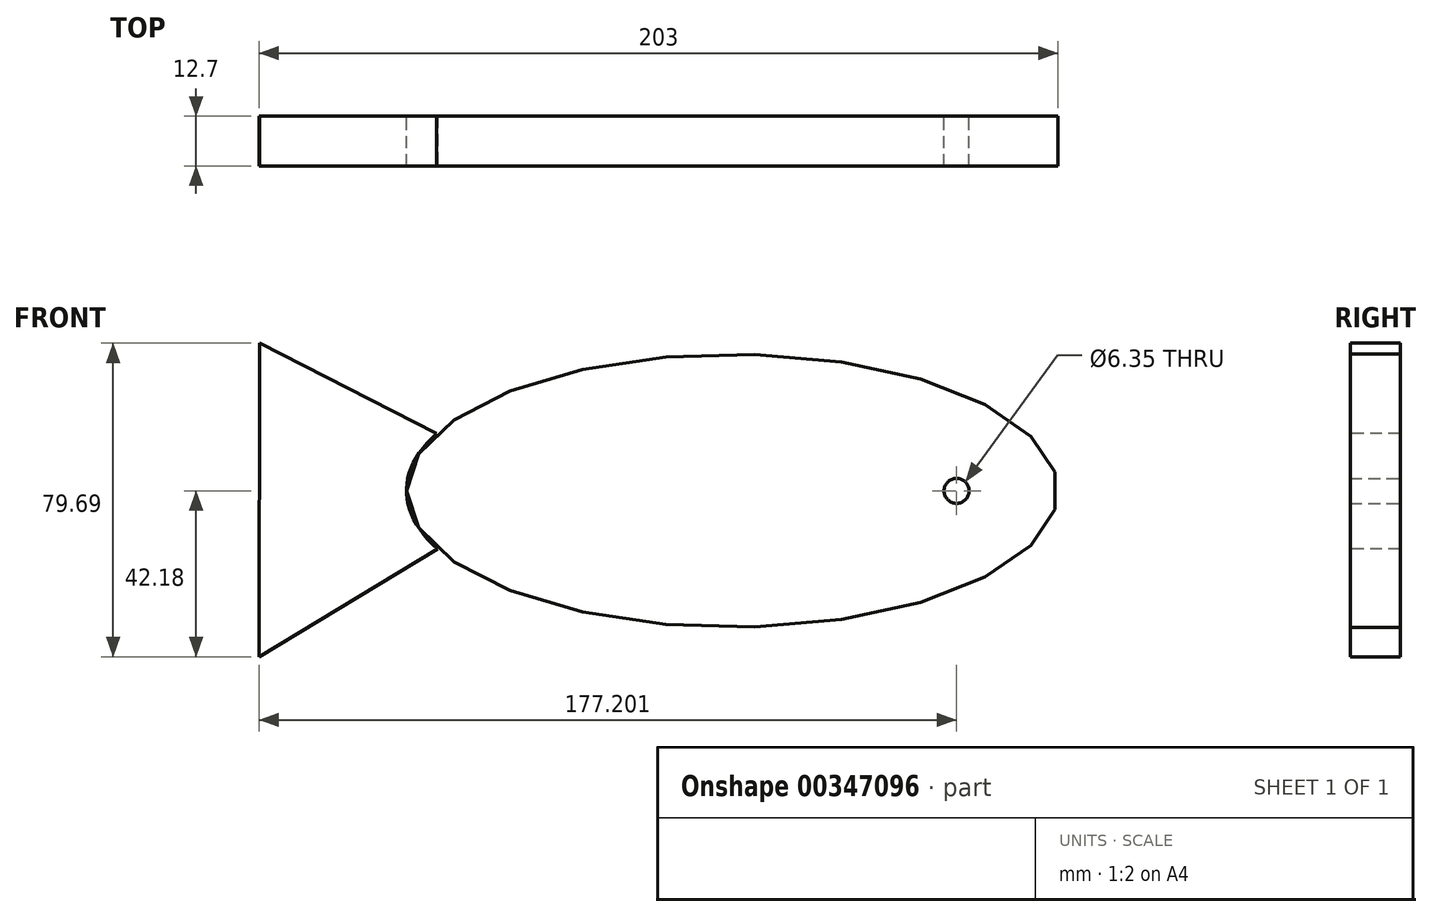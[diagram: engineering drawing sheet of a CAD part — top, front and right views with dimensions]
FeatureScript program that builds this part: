
annotation { "Feature Type Name" : "Feature", "Feature Type Description" : "" }
export const myFeature = defineFeature(function(context is Context, id is Id, definition is map)
    precondition{}
    {
        {
            var Q0;
            Q0=qCreatedBy(makeId("Front.planeOp"),FACE);
            var sketch = newSketch(context, id + "F0", { "sketchPlane" : qUnion([Q0])});
            skEllipse(sketch, "E0", {"center": v(49.64, 0) * mm, "majorRadius": 82.79 * mm, "minorRadius": 34.71 * mm, "majorAxis": v(-1, 0)});
            skSolve(sketch);
        }
        {
            var Q0;
            Q0=makeQuery(id+"F0.imprint","IMPRINT",FACE,{"disambiguationData":[TD([[makeQuery(id+"F0.imprint","IMPRINT",EDGE,{"derivedFrom":sQuery(id+"F0.wireOp",EDGE,"E0")}),1.0]])]});
            extrude(context, id + "F1", {"entities" : qUnion([Q0]), "depth" : 12.7 * mm});
        }
        {
            var Q0;
            Q0=makeQuery(id+"F1.opExtrude","CAP_FACE",FACE,{"disambiguationData":[OSD([sQuery(id+"F0.wireOp",EDGE,"E0")])],"isStart":false});
            var sketch = newSketch(context, id + "F2", { "sketchPlane" : qUnion([Q0])});
            skLineSegment(sketch, "E1", {"start": v(-70.57, -42.18) * mm, "end": v(0.97, 1.05) * mm});
            skLineSegment(sketch, "E2", {"start": v(0.97, 1.05) * mm, "end": v(-70.47, 37.5) * mm});
            skLineSegment(sketch, "E3", {"start": v(-70.47, 37.5) * mm, "end": v(-70.57, -42.18) * mm});
            skSolve(sketch);
        }
        {
            var Q0;
            {var subQ0=sQuery(id+"F2.wireOp",EDGE,"E3");Q0=makeQuery(id+"F2.imprint","IMPRINT",FACE,{"disambiguationData":[TD([[makeQuery(id+"F2.imprint","IMPRINT",EDGE,{"derivedFrom":subQ0}),1.0]])]});}
            extrude(context, id + "F3", {"entities" : qUnion([Q0]), "oppositeDirection" : true, "depth" : 12.7 * mm});
        }
        {
            var Q0;
            Q0=makeQuery(id+"F1.opExtrude","CAP_FACE",FACE,{"disambiguationData":[OSD([sQuery(id+"F0.wireOp",EDGE,"E0")])],"isStart":true});
            var sketch = newSketch(context, id + "F4", { "sketchPlane" : qUnion([Q0])});
            skPoint(sketch, "E4", {"position": v(-106.63, 0) * mm});
            skSolve(sketch);
        }
        {
            var Q0;
            Q0=sQuery(id+"F4.wireOp",VERTEX,"E4");
            var Q1;
            Q1=makeQuery(id+"F1.opExtrude","SWEPT_BODY",BODY,{"disambiguationData":[OSD([sQuery(id+"F0.wireOp",EDGE,"E0")])]});
            hole(context, id + "F5", {"style" : HoleStyle.SIMPLE, "endStyle" : HoleEndStyle.THROUGH, "holeDiameter" : 6.35 * mm, "isTappedThrough" : true, "tappedDepth" : 12.7 * mm, "tapClearance" : 3, "locations" : qUnion([Q0]), "scope" : qUnion([Q1])});
        }
    });
